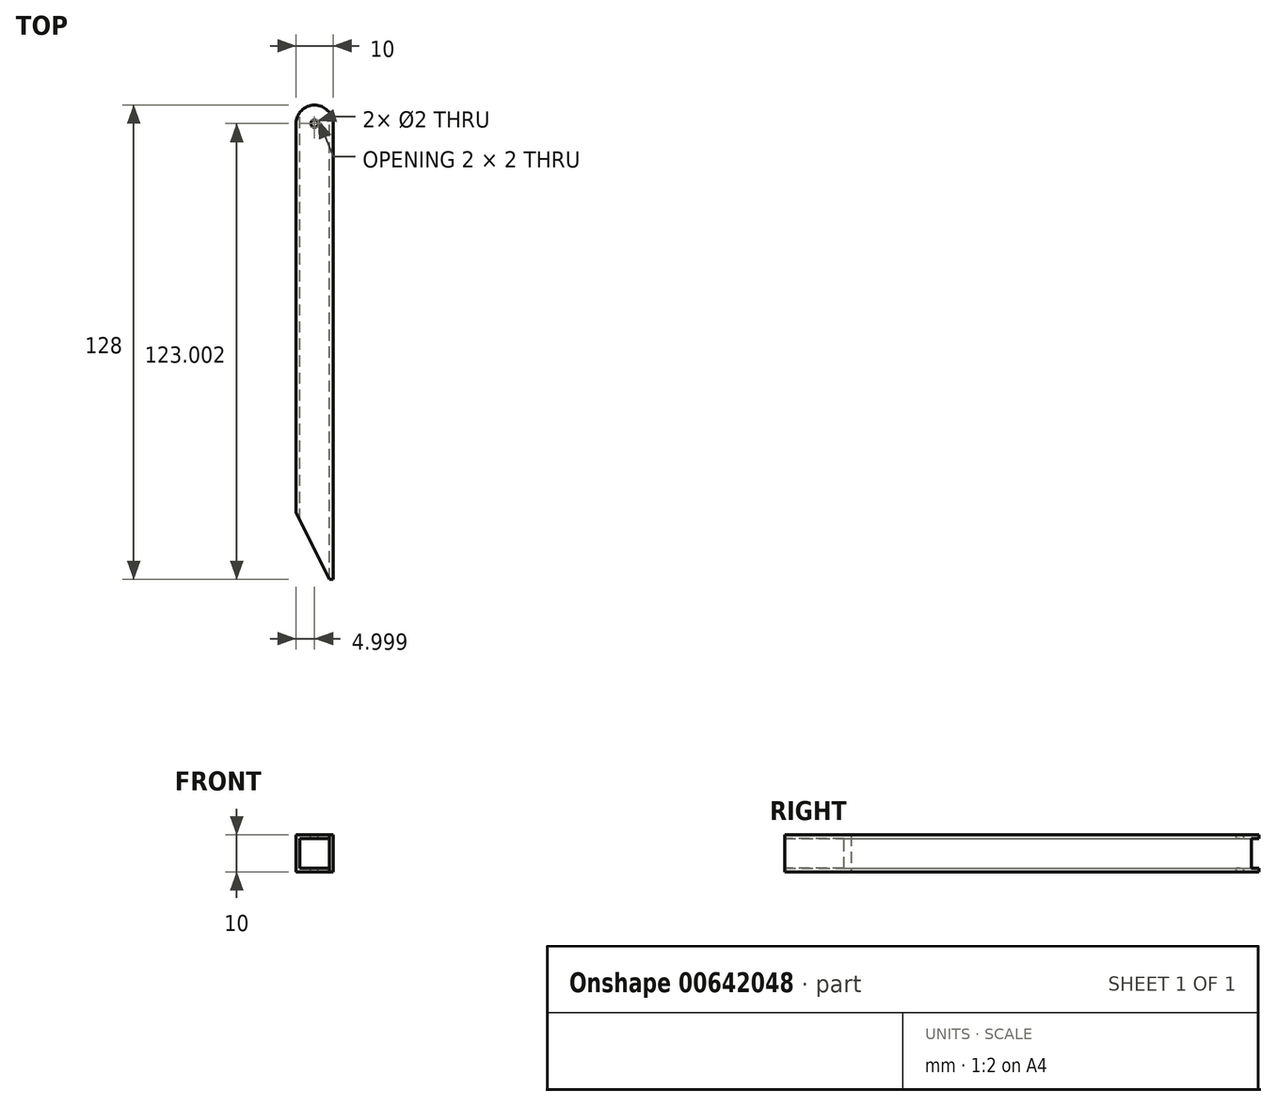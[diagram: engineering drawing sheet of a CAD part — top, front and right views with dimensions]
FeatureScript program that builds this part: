
annotation { "Feature Type Name" : "Feature", "Feature Type Description" : "" }
export const myFeature = defineFeature(function(context is Context, id is Id, definition is map)
    precondition{}
    {
        {
            var Q0;
            Q0=qCreatedBy(makeId("Top.planeOp"),FACE);
            var sketch = newSketch(context, id + "F0", { "sketchPlane" : qUnion([Q0])});
            skLineSegment(sketch, "E0.bottom", {"start": v(-1.6, 76.85) * mm, "end": v(8.4, 76.85) * mm});
            skLineSegment(sketch, "E0.left", {"start": v(-1.6, 76.85) * mm, "end": v(-1.6, -33.15) * mm});
            skLineSegment(sketch, "E0.right", {"start": v(8.4, 76.85) * mm, "end": v(8.4, -53.15) * mm});
            skLineSegment(sketch, "E1", {"start": v(8.4, -53.15) * mm, "end": v(-1.6, -33.15) * mm});
            skPoint(sketch, "E0.top.start.orphan", {"position": v(-1.6, -53.15) * mm});
            skSolve(sketch);
        }
        {
            var Q0;
            Q0=makeQuery(id+"F0.imprint","IMPRINT",FACE,{"disambiguationData":[TD([[makeQuery(id+"F0.imprint","IMPRINT",EDGE,{"derivedFrom":sQuery(id+"F0.wireOp",EDGE,"E0.bottom")}),-1.0]])]});
            extrude(context, id + "F1", {"entities" : qUnion([Q0]), "depth" : 10 * mm, "offsetDistance" : 25 * mm});
        }
        {
            var Q0;
            Q0=makeQuery(id+"F1.opExtrude","SWEPT_FACE",FACE,{"disambiguationData":[OSD([sQuery(id+"F0.wireOp",EDGE,"E0.bottom")])]});
            var sketch = newSketch(context, id + "F2", { "sketchPlane" : qUnion([Q0])});
            skLineSegment(sketch, "E2.bottom", {"start": v(-7.4, 9) * mm, "end": v(0.6, 9) * mm});
            skLineSegment(sketch, "E2.top", {"start": v(-7.4, 1) * mm, "end": v(0.6, 1) * mm});
            skLineSegment(sketch, "E2.left", {"start": v(-7.4, 9) * mm, "end": v(-7.4, 1) * mm});
            skLineSegment(sketch, "E2.right", {"start": v(0.6, 9) * mm, "end": v(0.6, 1) * mm});
            skSolve(sketch);
        }
        {
            var Q0;
            Q0=makeQuery(id+"F2.imprint","IMPRINT",FACE,{"disambiguationData":[TD([[makeQuery(id+"F2.imprint","IMPRINT",EDGE,{"derivedFrom":sQuery(id+"F2.wireOp",EDGE,"E2.bottom")}),-1.0]])]});
            extrude(context, id + "F3", {"entities" : qUnion([Q0]), "operationType" : NewBodyOperationType.REMOVE, "oppositeDirection" : true, "depth" : 150 * mm, "offsetDistance" : 25 * mm});
        }
        {
            var Q0;
            Q0=makeQuery(id+"F1.opExtrude","CAP_FACE",FACE,{"disambiguationData":[OSD([sQuery(id+"F0.wireOp",EDGE,"E0.bottom"),sQuery(id+"F0.wireOp",EDGE,"E0.left"),sQuery(id+"F0.wireOp",EDGE,"E0.right"),sQuery(id+"F0.wireOp",EDGE,"E1")])],"isStart":false});
            var sketch = newSketch(context, id + "F4", { "sketchPlane" : qUnion([Q0])});
            skArc(sketch, "E3", {"start": v(8.4, 71.85) * mm, "mid": v(3.4, 76.85) * mm, "end": v(-1.6, 71.85) * mm});
            skLineSegment(sketch, "E4", {"start": v(8.4, 71.85) * mm, "end": v(14.62, 71.85) * mm});
            skLineSegment(sketch, "E5", {"start": v(14.62, 71.85) * mm, "end": v(14.62, 78.7) * mm});
            skLineSegment(sketch, "E6", {"start": v(14.62, 78.7) * mm, "end": v(-2.96, 78.07) * mm});
            skLineSegment(sketch, "E7", {"start": v(-2.96, 78.07) * mm, "end": v(-2.74, 71.85) * mm});
            skLineSegment(sketch, "E8", {"start": v(-2.74, 71.85) * mm, "end": v(-1.6, 71.85) * mm});
            skCircle(sketch, "E9", {"center": v(3.4, 71.85) * mm, "radius": 1 * mm});
            skSolve(sketch);
        }
        {
            var Q0;
            Q0 = qSketchRegion(id + "F4", true);
            extrude(context, id + "F5", {"entities" : qUnion([Q0]), "operationType" : NewBodyOperationType.REMOVE, "oppositeDirection" : true, "depth" : 25 * mm, "offsetDistance" : 25 * mm});
        }
        {
            var Q0;
            Q0=makeQuery(id+"F1.opExtrude","SWEPT_FACE",FACE,{"disambiguationData":[OSD([sQuery(id+"F0.wireOp",EDGE,"E0.right")])]});
            var sketch = newSketch(context, id + "F6", { "sketchPlane" : qUnion([Q0])});
            skLineSegment(sketch, "E10.bottom", {"start": v(-54.23, 19.79) * mm, "end": v(-51.15, 19.79) * mm});
            skLineSegment(sketch, "E10.top", {"start": v(-54.23, -10.1) * mm, "end": v(-51.15, -10.1) * mm});
            skLineSegment(sketch, "E10.left", {"start": v(-54.23, 19.79) * mm, "end": v(-54.23, -10.1) * mm});
            skLineSegment(sketch, "E10.right", {"start": v(-51.15, 19.79) * mm, "end": v(-51.15, -10.1) * mm});
            skSolve(sketch);
        }
        {
            var Q0;
            {var subQ1=sQuery(id+"F6.wireOp",EDGE,"E10.bottom");Q0=makeQuery(id+"F6.imprint","IMPRINT",FACE,{"disambiguationData":[TD([[makeQuery(id+"F6.imprint","IMPRINT",EDGE,{"derivedFrom":subQ1}),-1.0]])]});}
            var Q1;
            {var subQ1=sQuery(id+"F0.wireOp",EDGE,"E0.right");var subQ6=makeQuery(id+"F1.opExtrude","SWEPT_EDGE",EDGE,{"disambiguationData":[OSD([subQ1,sQuery(id+"F0.wireOp",EDGE,"E1")])]});Q1=makeQuery(id+"F6.imprint","IMPRINT",FACE,{"disambiguationData":[TD([[makeQuery(id+"F6.imprint","IMPRINT",EDGE,{"derivedFrom":subQ6}),1.0]])]});}
            extrude(context, id + "F7", {"entities" : qUnion([Q0, Q1]), "operationType" : NewBodyOperationType.REMOVE, "oppositeDirection" : true, "depth" : 25 * mm, "offsetDistance" : 25 * mm});
        }
    });
